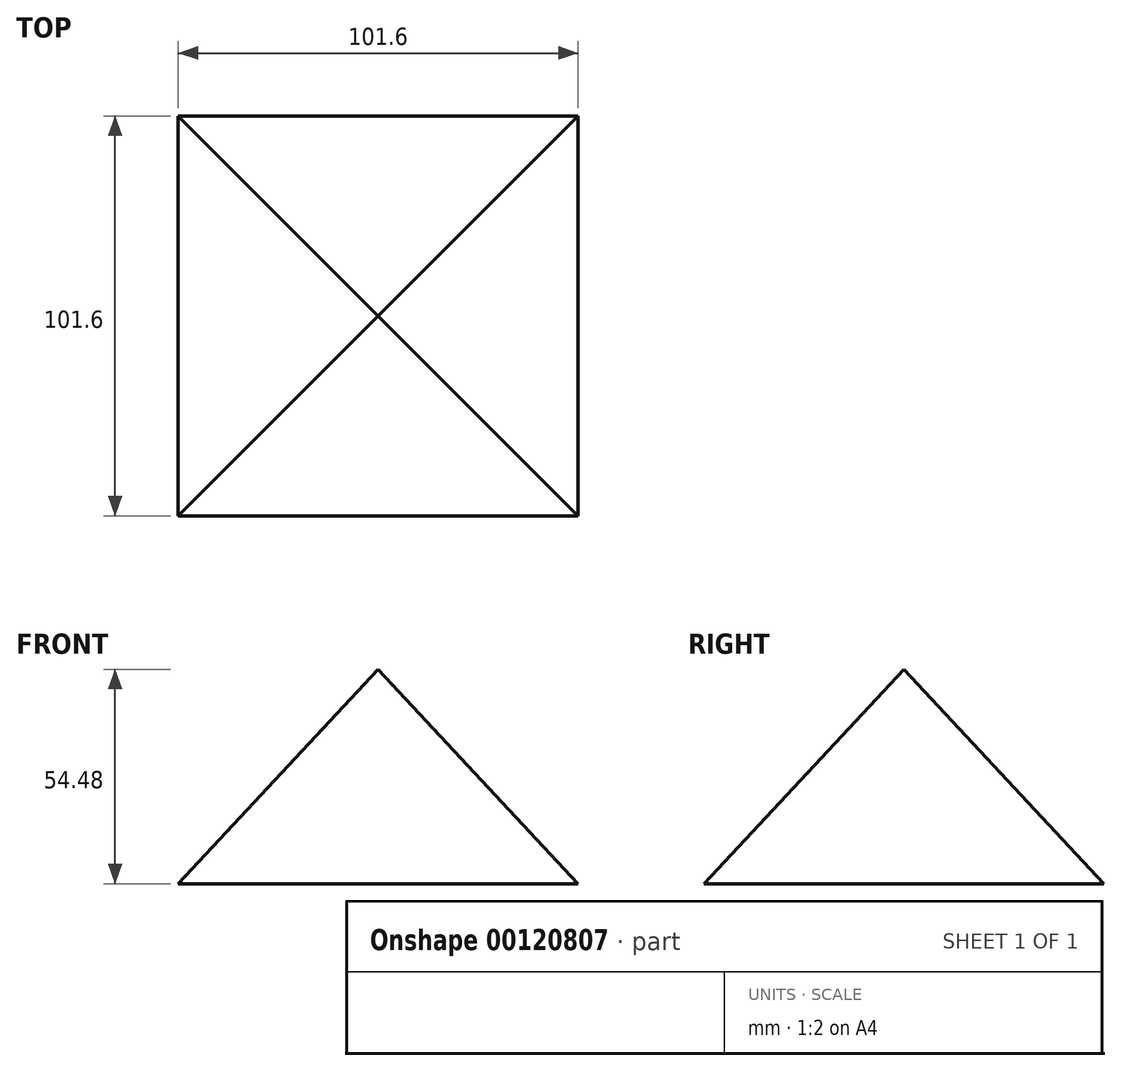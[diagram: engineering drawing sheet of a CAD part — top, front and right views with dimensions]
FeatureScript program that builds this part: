
annotation { "Feature Type Name" : "Feature", "Feature Type Description" : "" }
export const myFeature = defineFeature(function(context is Context, id is Id, definition is map)
    precondition{}
    {
        {
            var Q0;
            Q0=qCreatedBy(makeId("Top.planeOp"),FACE);
            var sketch = newSketch(context, id + "F0", { "sketchPlane" : qUnion([Q0])});
            skLineSegment(sketch, "E0.bottom", {"start": v(-68.63, -62.36) * mm, "end": v(32.97, -62.36) * mm});
            skLineSegment(sketch, "E0.top", {"start": v(-68.63, 39.24) * mm, "end": v(32.97, 39.24) * mm});
            skLineSegment(sketch, "E0.left", {"start": v(-68.63, -62.36) * mm, "end": v(-68.63, 39.24) * mm});
            skLineSegment(sketch, "E0.right", {"start": v(32.97, -62.36) * mm, "end": v(32.97, 39.24) * mm});
            skSolve(sketch);
        }
        {
            var Q0;
            Q0=qSketchRegion(id+"F0",true);
            extrude(context, id + "F1", {"entities" : qUnion([Q0]), "depth" : 304.8 * mm, "hasDraft" : true, "draftAngle" : 43 * degree, "draftPullDirection" : true});
        }
    });
